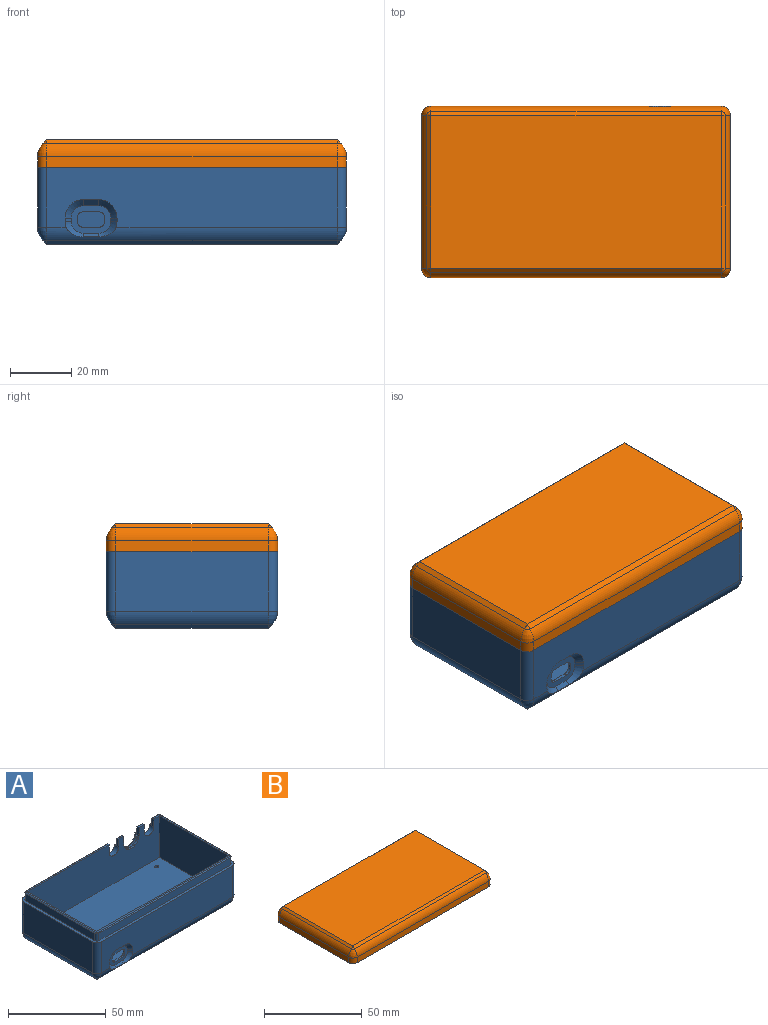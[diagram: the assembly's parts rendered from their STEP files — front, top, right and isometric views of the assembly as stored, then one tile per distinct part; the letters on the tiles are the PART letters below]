
ASSEMBLY  parts=2 mates=1
PART A: 91 faces, bbox 101x56x30 mm
  f0: plane 95x19.51mm, normal (0,-1,0), area 1716.6mm2, adj f18,f49,f50,f52,f53,f54,f55,f56
  f1: plane 5x1mm, normal (0,0,-1), area 5mm2, adj f5,f43,f44,f47
  f2: plane 1x1mm, normal (1,0,0), area 1mm2, adj f5,f43,f44,f45
  f3: plane 5x1mm, normal (0,0,1), area 5mm2, adj f5,f43,f45,f46
  f4: plane 1x1mm, normal (-1,0,0), area 1mm2, adj f5,f43,f46,f47
  f5: plane 95x26mm, normal (0,1,0), area 2428.4mm2, adj f1,f2,f3,f4,f15,f22,f24,f25
  f6: plane 1x0.51mm, normal (0,0,1), area 0.5mm2, adj f9,f32,f41,f42
  f7: plane 1x0.51mm, normal (0,0,1), area 0.5mm2, adj f9,f32,f41,f42
  f8: plane 95x26mm, normal (0,-1,0), area 2259mm2, adj f14,f15,f16,f22,f24,f25,f32,f33
  f9: cylinder r=5mm len=9.89mm, axis (0,1,0), area 14.2mm2, adj f6,f7,f41,f42
  f10: plane 4.5x3.75mm, normal (0,1,0), area 16.9mm2, adj f17,f34,f39,f89
  f11: plane 4.5x3.75mm, normal (0,1,0), area 16.9mm2, adj f18,f40,f79,f80
  f12: plane 58.75x4.5mm, normal (0,1,0), area 264.4mm2, adj f18,f36,f76,f88
  f13: plane 4.5x3.75mm, normal (0,1,0), area 16.9mm2, adj f19,f33,f37,f90
  f14: plane 3.75x1mm, normal (0,0,1), area 3.7mm2, adj f8,f34,f39,f89
  f15: plane 97x52mm, normal (0,0,1), area 260.6mm2, adj f5,f8,f24,f25,f36,f40,f80,f81
  f16: plane 3.75x1mm, normal (0,0,1), area 3.7mm2, adj f8,f33,f37,f90
  f17: plane 3.75x1.5mm, normal (0,0,1), area 5.6mm2, adj f10,f29,f32,f38
  f18: plane 101x56mm, normal (0,0,1), area 407.5mm2, adj f0,f11,f12,f26,f27,f28,f29,f30
  f19: plane 3.75x1.5mm, normal (0,0,1), area 5.6mm2, adj f13,f29,f32,f35
  f20: cylinder r=1mm len=4mm, axis (0,0,-1), area 25.1mm2, adj f22,f23
  f21: cylinder r=1mm len=4mm, axis (0,0,-1), area 25.1mm2, adj f22,f23
  f22: plane 95x50mm, normal (0,0,1), area 4743.7mm2, adj f5,f8,f20,f21,f24,f25
  f23: plane 95x50mm, normal (0,0,-1), area 4743.7mm2, adj f20,f21,f60,f63,f64,f67
  f24: plane 50x26mm, normal (1,0,0), area 1300mm2, adj f5,f8,f15,f22
  f25: plane 50x26mm, normal (-1,0,0), area 1300mm2, adj f5,f8,f15,f22
  f26: plane 50x4.5mm, normal (-1,0,0), area 225mm2, adj f18,f76,f77,f86
  f27: plane 95x4.5mm, normal (0,-1,0), area 427.5mm2, adj f18,f77,f78,f84
  f28: plane 50x4.5mm, normal (1,0,0), area 225mm2, adj f18,f78,f79,f82
  f29: plane 95x19.51mm, normal (0,1,0), area 1767.9mm2, adj f17,f18,f19,f32,f35,f38,f48,f51
  f30: plane 50x19.51mm, normal (-1,0,0), area 975.7mm2, adj f18,f48,f49,f72
  f31: plane 50x19.51mm, normal (1,0,0), area 975.7mm2, adj f18,f50,f51,f71
  f32: cylinder r=5.5mm len=11mm, axis (0,1,0), area 36.1mm2, adj f6,f7,f8,f17,f19,f29,f33,f34
  f33: plane 5x1.5mm, normal (1,0,0), area 7.4mm2, adj f8,f13,f16,f32,f90
  f34: plane 5x1.5mm, normal (-1,0,0), area 7.4mm2, adj f8,f10,f14,f32,f89
  f35: cylinder r=3.5mm len=7mm, axis (0,1,0), area 33mm2, adj f8,f18,f19,f29,f36,f37
  f36: plane 5x1.5mm, normal (1,0,0), area 7.4mm2, adj f8,f12,f15,f35,f88
  f37: plane 5x1.5mm, normal (-1,0,0), area 7.4mm2, adj f8,f13,f16,f35,f90
  f38: cylinder r=3.5mm len=7mm, axis (0,1,0), area 33mm2, adj f8,f17,f18,f29,f39,f40
  f39: plane 5x1.5mm, normal (1,0,0), area 7.4mm2, adj f8,f10,f14,f38,f89
  f40: plane 5x1.5mm, normal (-1,0,0), area 7.4mm2, adj f8,f11,f15,f38,f80
  f41: plane 10.9x4.75mm, normal (0,1,0), area 7.5mm2, adj f6,f7,f9,f32
  f42: plane 10.9x4.75mm, normal (0,-1,0), area 7.5mm2, adj f6,f7,f9,f32
  f43: plane 13x9mm, normal (0,-1,0), area 61.7mm2, adj f1,f2,f3,f4,f44,f45,f46,f47
  f44: cylinder r=2mm len=2mm, axis (0,-1,0), area 3.1mm2, adj f1,f2,f5,f43
  f45: cylinder r=2mm len=2mm, axis (0,1,0), area 3.1mm2, adj f2,f3,f5,f43
  f46: cylinder r=2mm len=2mm, axis (0,-1,0), area 3.1mm2, adj f3,f4,f5,f43
  f47: cylinder r=2mm len=2mm, axis (0,1,0), area 3.1mm2, adj f1,f4,f5,f43
  f48: cylinder r=3mm len=19.51mm, axis (0,0,1), area 92mm2, adj f18,f29,f30,f74
  f49: cylinder r=3mm len=19.51mm, axis (0,0,-1), area 92mm2, adj f0,f18,f30,f70
  f50: cylinder r=3mm len=19.51mm, axis (0,0,1), area 92mm2, adj f0,f18,f31,f69
  f51: cylinder r=3mm len=19.51mm, axis (0,0,-1), area 92mm2, adj f18,f29,f31,f73
  f52: plane 5x2mm, normal (0,-0.71,-0.71), area 14.1mm2, adj f0,f43,f53,f54
  f53: cone r=6mm half-angle=45deg, axis (0,-1,0), area 22.2mm2, adj f0,f43,f52,f55
  f54: cone r=6mm half-angle=45deg, axis (0,-1,0), area 22.2mm2, adj f0,f43,f52,f56
  f55: plane 2x2mm, normal (0.71,-0.71,0), area 2.8mm2, adj f0,f43,f53,f57
  f56: plane 2x2mm, normal (-0.71,-0.71,0), area 2.8mm2, adj f0,f43,f54,f58
  f57: cone r=6mm half-angle=45deg, axis (0,-1,0), area 17.5mm2, adj f0,f43,f55,f59,f68
  f58: cone r=6mm half-angle=45deg, axis (0,-1,0), area 17.5mm2, adj f0,f43,f56,f59,f68
  f59: plane 5x1.13mm, normal (0,-0.71,0.71), area 8mm2, adj f43,f57,f58,f68
  f60: plane 95x1.24mm, normal (0,-0.71,-0.71), area 166.9mm2, adj f23,f61,f62,f68
  f61: cone r=3mm half-angle=45deg, axis (0,0,1), area 1.7mm2, adj f60,f63,f70
  f62: cone r=3mm half-angle=45deg, axis (0,0,1), area 1.7mm2, adj f60,f64,f69
  f63: plane 50x1.24mm, normal (-0.71,0,-0.71), area 87.9mm2, adj f23,f61,f65,f72
  f64: plane 50x1.24mm, normal (0.71,0,-0.71), area 87.9mm2, adj f23,f62,f66,f71
  f65: cone r=3mm half-angle=45deg, axis (0,0,1), area 1.7mm2, adj f63,f67,f74
  f66: cone r=3mm half-angle=45deg, axis (0,0,1), area 1.7mm2, adj f64,f67,f73
  f67: plane 95x1.24mm, normal (0,0.71,-0.71), area 166.9mm2, adj f23,f65,f66,f75
  f68: cylinder r=6mm len=95mm, axis (1,0,0), area 404.2mm2, adj f0,f57,f58,f59,f60,f69,f70
  f69: revolved ~4.24x3mm, area 17.8mm2, adj f50,f62,f68,f71
  f70: revolved ~4.24x3mm, area 17.8mm2, adj f49,f61,f68,f72
  f71: cylinder r=6mm len=50mm, axis (0,1,0), area 235.6mm2, adj f31,f64,f69,f73
  f72: cylinder r=6mm len=50mm, axis (0,-1,0), area 235.6mm2, adj f30,f63,f70,f74
  f73: revolved ~4.24x3mm, area 17.8mm2, adj f51,f66,f71,f75
  f74: revolved ~4.24x3mm, area 17.8mm2, adj f48,f65,f72,f75
  f75: cylinder r=6mm len=95mm, axis (-1,0,0), area 447.7mm2, adj f29,f67,f73,f74
  f76: cylinder r=1.5mm len=4.5mm, axis (0,0,1), area 10.6mm2, adj f12,f18,f26,f87
  f77: cylinder r=1.5mm len=4.5mm, axis (0,0,-1), area 10.6mm2, adj f18,f26,f27,f85
  f78: cylinder r=1.5mm len=4.5mm, axis (0,0,1), area 10.6mm2, adj f18,f27,f28,f83
  f79: cylinder r=1.5mm len=4.5mm, axis (0,0,-1), area 10.6mm2, adj f11,f18,f28,f81
  f80: plane 3.75x0.5mm, normal (0,0.71,0.71), area 2.7mm2, adj f11,f15,f40,f81
  f81: cone r=1mm half-angle=45deg, axis (0,0,-1), area 1.4mm2, adj f15,f79,f80,f82
  f82: plane 50x0.5mm, normal (0.71,0,0.71), area 35.4mm2, adj f15,f28,f81,f83
  f83: cone r=1mm half-angle=45deg, axis (0,0,-1), area 1.4mm2, adj f15,f78,f82,f84
  f84: plane 95x0.5mm, normal (0,-0.71,0.71), area 67.2mm2, adj f15,f27,f83,f85
  f85: cone r=1mm half-angle=45deg, axis (0,0,-1), area 1.4mm2, adj f15,f77,f84,f86
  f86: plane 50x0.5mm, normal (-0.71,0,0.71), area 35.4mm2, adj f15,f26,f85,f87
  f87: cone r=1mm half-angle=45deg, axis (0,0,-1), area 1.4mm2, adj f15,f76,f86,f88
  f88: plane 58.75x0.5mm, normal (0,0.71,0.71), area 41.5mm2, adj f12,f15,f36,f87
  f89: plane 3.75x0.5mm, normal (0,0.71,0.71), area 2.7mm2, adj f10,f14,f34,f39
  f90: plane 3.75x0.5mm, normal (0,0.71,0.71), area 2.7mm2, adj f13,f16,f33,f37
PART B: 64 faces, bbox 101x56x9 mm
  f0: plane 70.77x3.51mm, normal (0,1,0), area 226.4mm2, adj f4,f14,f22,f25,f29,f48
  f1: plane 95x1mm, normal (0,-1,0), area 93.5mm2, adj f2,f15,f16,f18,f27
  f2: plane 98x53mm, normal (0,0,-1), area 437.5mm2, adj f1,f3,f6,f7,f8,f9,f15,f16
  f3: plane 20x4.5mm, normal (0,-1,0), area 57mm2, adj f2,f21,f22,f23,f24,f50,f53,f63
  f4: plane 101x56mm, normal (0,0,-1), area 273.2mm2, adj f0,f10,f11,f12,f13,f24,f25,f29
  f5: plane 3.75x1mm, normal (0,0,-1), area 3.8mm2, adj f10,f22,f24,f63
  f6: plane 50x4.5mm, normal (1,0,0), area 225mm2, adj f2,f49,f52,f59
  f7: plane 75x4.5mm, normal (0,-1,0), area 304.5mm2, adj f2,f20,f22,f23,f25,f49,f61,f62
  f8: plane 50x4.5mm, normal (-1,0,0), area 225mm2, adj f2,f50,f51,f55
  f9: plane 95x4.5mm, normal (0,1,0), area 427.5mm2, adj f2,f51,f52,f57
  f10: plane 15.77x3.51mm, normal (0,1,0), area 33.1mm2, adj f4,f5,f22,f24,f32,f48
  f11: plane 50x3.51mm, normal (-1,0,0), area 175.7mm2, adj f4,f29,f30,f44
  f12: plane 95x3.51mm, normal (0,-1,0), area 333.9mm2, adj f4,f30,f31,f41
  f13: plane 50x3.51mm, normal (1,0,0), area 175.7mm2, adj f4,f31,f32,f45
  f14: plane 3.75x1mm, normal (0,0,-1), area 3.8mm2, adj f0,f22,f25,f62
  f15: plane 50x1mm, normal (-1,0,0), area 50mm2, adj f1,f2,f17,f18
  f16: plane 50x1mm, normal (1,0,0), area 50mm2, adj f1,f2,f17,f18
  f17: plane 95x1mm, normal (0,1,0), area 95mm2, adj f2,f15,f16,f18
  f18: plane 95x50mm, normal (0,0,-1), area 4750mm2, adj f1,f15,f16,f17
  f19: plane 95x50mm, normal (0,0,1), area 4750mm2, adj f33,f36,f37,f40
  f20: plane 0.51x0.5mm, normal (0,0,-1), area 0.3mm2, adj f7,f22,f23,f26
  f21: plane 0.51x0.5mm, normal (0,0,-1), area 0.3mm2, adj f3,f22,f23,f26
  f22: cylinder r=5.5mm len=11mm, axis (0,1,0), area 16.1mm2, adj f0,f3,f5,f7,f10,f14,f20,f21
  f23: cylinder r=5mm len=9.89mm, axis (0,1,0), area 7.1mm2, adj f3,f7,f20,f21,f26
  f24: cylinder r=3.5mm len=7mm, axis (0,1,0), area 16.2mm2, adj f3,f4,f5,f10,f53,f63
  f25: cylinder r=3.5mm len=7mm, axis (0,1,0), area 16.2mm2, adj f0,f4,f7,f14,f61,f62
  f26: plane 10.9x4.75mm, normal (0,1,0), area 7.5mm2, adj f20,f21,f22,f23
  f27: cylinder r=5.5mm len=4.58mm, axis (0,-1,0), area 4.7mm2, adj f1,f2,f28
  f28: plane 4.58x0.5mm, normal (0,-1,0), area 1.5mm2, adj f2,f27
  f29: cylinder r=3mm len=3.51mm, axis (0,0,1), area 16.6mm2, adj f0,f4,f11,f46
  f30: cylinder r=3mm len=3.51mm, axis (0,0,-1), area 16.6mm2, adj f4,f11,f12,f42
  f31: cylinder r=3mm len=3.51mm, axis (0,0,1), area 16.6mm2, adj f4,f12,f13,f43
  f32: cylinder r=3mm len=3.51mm, axis (0,0,-1), area 16.6mm2, adj f4,f10,f13,f47
  f33: plane 95x1.24mm, normal (0,-0.71,0.71), area 166.9mm2, adj f19,f34,f35,f41
  f34: cone r=3mm half-angle=45deg, axis (0,0,-1), area 1.7mm2, adj f33,f36,f42
  f35: cone r=3mm half-angle=45deg, axis (0,0,-1), area 1.7mm2, adj f33,f37,f43
  f36: plane 50x1.24mm, normal (-0.71,0,0.71), area 87.9mm2, adj f19,f34,f38,f44
  f37: plane 50x1.24mm, normal (0.71,0,0.71), area 87.9mm2, adj f19,f35,f39,f45
  f38: cone r=3mm half-angle=45deg, axis (0,0,-1), area 1.7mm2, adj f36,f40,f46
  f39: cone r=3mm half-angle=45deg, axis (0,0,-1), area 1.7mm2, adj f37,f40,f47
  f40: plane 95x1.24mm, normal (0,0.71,0.71), area 166.9mm2, adj f19,f38,f39,f48
  f41: cylinder r=6mm len=95mm, axis (1,0,0), area 447.7mm2, adj f12,f33,f42,f43
  f42: revolved ~4.24x3mm, area 17.8mm2, adj f30,f34,f41,f44
  f43: revolved ~4.24x3mm, area 17.8mm2, adj f31,f35,f41,f45
  f44: cylinder r=6mm len=50mm, axis (0,-1,0), area 235.6mm2, adj f11,f36,f42,f46
  f45: cylinder r=6mm len=50mm, axis (0,1,0), area 235.6mm2, adj f13,f37,f43,f47
  f46: revolved ~4.24x3mm, area 17.8mm2, adj f29,f38,f44,f48
  f47: revolved ~4.24x3mm, area 17.8mm2, adj f32,f39,f45,f48
  f48: cylinder r=6mm len=95mm, axis (-1,0,0), area 435.8mm2, adj f0,f10,f22,f40,f46,f47
  f49: cylinder r=1.5mm len=4.5mm, axis (0,0,-1), area 10.6mm2, adj f2,f6,f7,f60
  f50: cylinder r=1.5mm len=4.5mm, axis (0,0,1), area 10.6mm2, adj f2,f3,f8,f54
  f51: cylinder r=1.5mm len=4.5mm, axis (0,0,-1), area 10.6mm2, adj f2,f8,f9,f56
  f52: cylinder r=1.5mm len=4.5mm, axis (0,0,1), area 10.6mm2, adj f2,f6,f9,f58
  f53: plane 3.79x0.5mm, normal (0,-0.71,-0.71), area 2.7mm2, adj f3,f4,f24,f54
  f54: cone r=2mm half-angle=45deg, axis (0,0,-1), area 1.9mm2, adj f4,f50,f53,f55
  f55: plane 50x0.5mm, normal (-0.71,0,-0.71), area 35.4mm2, adj f4,f8,f54,f56
  f56: cone r=2mm half-angle=45deg, axis (0,0,-1), area 1.9mm2, adj f4,f51,f55,f57
  f57: plane 95x0.5mm, normal (0,0.71,-0.71), area 67.2mm2, adj f4,f9,f56,f58
  f58: cone r=2mm half-angle=45deg, axis (0,0,-1), area 1.9mm2, adj f4,f52,f57,f59
  f59: plane 50x0.5mm, normal (0.71,0,-0.71), area 35.4mm2, adj f4,f6,f58,f60
  f60: cone r=2mm half-angle=45deg, axis (0,0,-1), area 1.9mm2, adj f4,f49,f59,f61
  f61: plane 58.79x0.5mm, normal (0,-0.71,-0.71), area 41.6mm2, adj f4,f7,f25,f60
  f62: plane 3.81x0.5mm, normal (0,-0.71,-0.71), area 2.7mm2, adj f7,f14,f22,f25
  f63: plane 3.81x0.5mm, normal (0,-0.71,-0.71), area 2.7mm2, adj f3,f5,f22,f24
PLACE A at identity fixed
PLACE B at identity
MATE slider B.f51 <-> A.f78  axis (0,0,-1) through (95,0,30)mm
